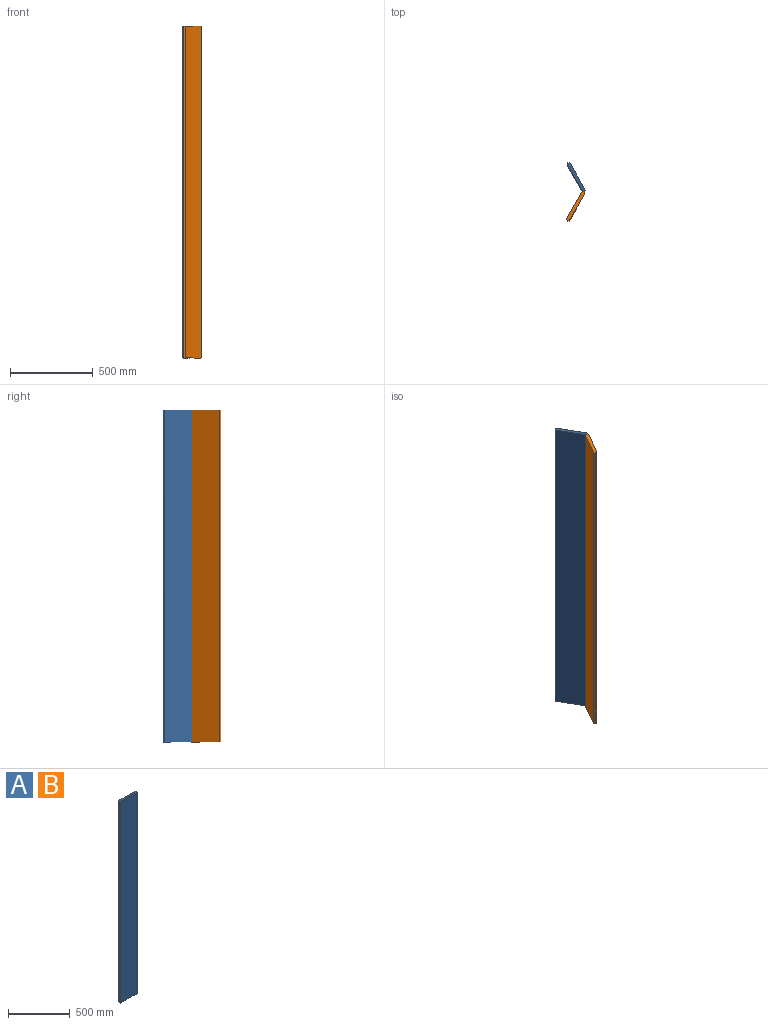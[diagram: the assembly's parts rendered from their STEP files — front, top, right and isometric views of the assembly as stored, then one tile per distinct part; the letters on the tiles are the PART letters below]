
ASSEMBLY  parts=2 mates=1
PART A: 8 faces, bbox 200x20x2000 mm
  f0: plane 2000x10mm, normal (-0.87,0.5,0), area 23094mm2, adj f1,f5,f6,f7
  f1: plane 2000x10mm, normal (-0.87,-0.5,0), area 23094mm2, adj f0,f2,f6,f7
  f2: plane 2000x188.45mm, normal (0,-1,0), area 376906mm2, adj f1,f3,f6,f7
  f3: plane 2000x10mm, normal (0.87,-0.5,0), area 23094mm2, adj f2,f4,f6,f7
  f4: plane 2000x10mm, normal (0.87,0.5,0), area 23094mm2, adj f3,f5,f6,f7
  f5: plane 2000x188.45mm, normal (0,1,0), area 376906mm2, adj f0,f4,f6,f7
  f6: plane 200x20mm, normal (0,0,1), area 3884.5mm2, adj f0,f1,f2,f3,f4,f5
  f7: plane 200x20mm, normal (0,0,-1), area 3884.5mm2, adj f0,f1,f2,f3,f4,f5
PART B: same geometry as A
PLACE A rot(axis=(0,0,-1),60deg) t=(-496.12,230.14,-308.74)mm
PLACE B rot(axis=(0,0,-1),120deg) t=(-499.59,56.93,-308.74)mm
MATE planar B.f1 <-> A.f3  axis (0,1,0) through (-455.37,143.53,691.26)mm
